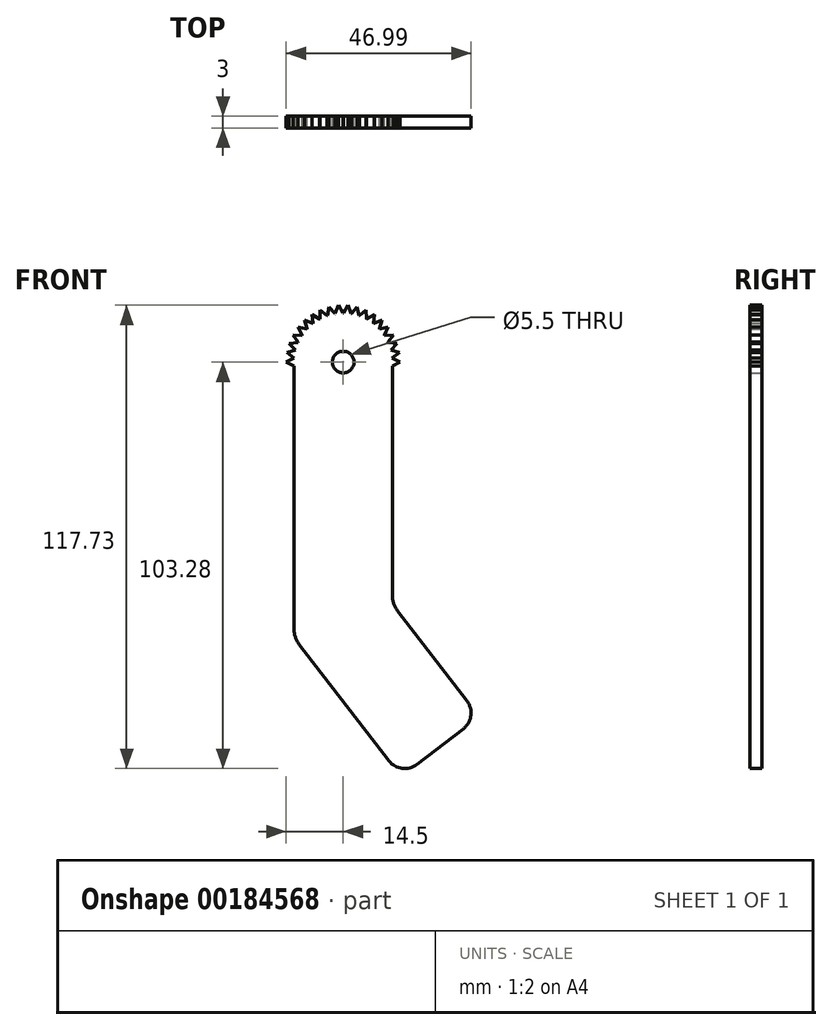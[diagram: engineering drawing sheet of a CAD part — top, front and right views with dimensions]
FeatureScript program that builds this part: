
annotation { "Feature Type Name" : "Feature", "Feature Type Description" : "" }
export const myFeature = defineFeature(function(context is Context, id is Id, definition is map)
    precondition{}
    {
        {
            var Q0;
            Q0=qCreatedBy(makeId("Front.planeOp"),FACE);
            var sketch = newSketch(context, id + "F0", { "sketchPlane" : qUnion([Q0])});
            skCircle(sketch, "E0", {"center": v(0, 0) * mm, "radius": 12.5 * mm});
            skLineSegment(sketch, "E1", {"start": v(-12.5, 0) * mm, "end": v(-12.5, -67.84) * mm});
            skLineSegment(sketch, "E2", {"start": v(-11.18, -71.71) * mm, "end": v(26.36, -120.4) * mm});
            skLineSegment(sketch, "E3", {"start": v(35.27, -121.56) * mm, "end": v(45.01, -114.05) * mm});
            skLineSegment(sketch, "E4", {"start": v(46.16, -105.14) * mm, "end": v(13.82, -63.2) * mm});
            skLineSegment(sketch, "E5", {"start": v(12.5, -59.32) * mm, "end": v(12.5, 0) * mm});
            skLineSegment(sketch, "E6", {"start": v(12.5, 0) * mm, "end": v(14.5, 0) * mm});
            skLineSegment(sketch, "E7", {"start": v(14.5, 0) * mm, "end": v(12.46, 1) * mm});
            skLineSegment(sketch, "E8", {"start": v(12.46, 1) * mm, "end": v(12.46, -1) * mm});
            skLineSegment(sketch, "E9", {"start": v(12.46, -1) * mm, "end": v(14.5, 0) * mm});
            skLineSegment(sketch, "E10.1.0", {"start": v(14.3, 2.39) * mm, "end": v(12.13, 3.04) * mm});
            skLineSegment(sketch, "E10.1.1", {"start": v(12.45, 1.06) * mm, "end": v(14.3, 2.39) * mm});
            skLineSegment(sketch, "E10.1.2", {"start": v(12.13, 3.04) * mm, "end": v(12.45, 1.06) * mm});
            skLineSegment(sketch, "E10.1.3", {"start": v(12.33, 2.06) * mm, "end": v(14.3, 2.39) * mm});
            skLineSegment(sketch, "E10.2.0", {"start": v(13.71, 4.7) * mm, "end": v(11.46, 5) * mm});
            skLineSegment(sketch, "E10.2.1", {"start": v(12.1, 3.1) * mm, "end": v(13.71, 4.7) * mm});
            skLineSegment(sketch, "E10.2.2", {"start": v(11.46, 5) * mm, "end": v(12.1, 3.1) * mm});
            skLineSegment(sketch, "E10.2.3", {"start": v(11.82, 4.06) * mm, "end": v(13.71, 4.7) * mm});
            skLineSegment(sketch, "E10.3.0", {"start": v(12.75, 6.9) * mm, "end": v(10.48, 6.8) * mm});
            skLineSegment(sketch, "E10.3.1", {"start": v(11.43, 5.05) * mm, "end": v(12.75, 6.9) * mm});
            skLineSegment(sketch, "E10.3.2", {"start": v(10.48, 6.8) * mm, "end": v(11.43, 5.05) * mm});
            skLineSegment(sketch, "E10.3.3", {"start": v(11, 5.95) * mm, "end": v(12.75, 6.9) * mm});
            skLineSegment(sketch, "E10.4.0", {"start": v(11.44, 8.9) * mm, "end": v(9.22, 8.44) * mm});
            skLineSegment(sketch, "E10.4.1", {"start": v(10.45, 6.86) * mm, "end": v(11.44, 8.9) * mm});
            skLineSegment(sketch, "E10.4.2", {"start": v(9.22, 8.44) * mm, "end": v(10.45, 6.86) * mm});
            skLineSegment(sketch, "E10.4.3", {"start": v(9.86, 7.68) * mm, "end": v(11.44, 8.9) * mm});
            skLineSegment(sketch, "E10.5.0", {"start": v(9.82, 10.67) * mm, "end": v(7.7, 9.84) * mm});
            skLineSegment(sketch, "E10.5.1", {"start": v(9.17, 8.49) * mm, "end": v(9.82, 10.67) * mm});
            skLineSegment(sketch, "E10.5.2", {"start": v(7.7, 9.84) * mm, "end": v(9.17, 8.49) * mm});
            skLineSegment(sketch, "E10.5.3", {"start": v(8.47, 9.2) * mm, "end": v(9.82, 10.67) * mm});
            skLineSegment(sketch, "E10.6.0", {"start": v(7.93, 12.14) * mm, "end": v(5.98, 10.98) * mm});
            skLineSegment(sketch, "E10.6.1", {"start": v(7.65, 9.88) * mm, "end": v(7.93, 12.14) * mm});
            skLineSegment(sketch, "E10.6.2", {"start": v(5.98, 10.98) * mm, "end": v(7.65, 9.88) * mm});
            skLineSegment(sketch, "E10.6.3", {"start": v(6.84, 10.46) * mm, "end": v(7.93, 12.14) * mm});
            skLineSegment(sketch, "E10.7.0", {"start": v(5.82, 13.28) * mm, "end": v(4.09, 11.81) * mm});
            skLineSegment(sketch, "E10.7.1", {"start": v(5.92, 11) * mm, "end": v(5.82, 13.28) * mm});
            skLineSegment(sketch, "E10.7.2", {"start": v(4.09, 11.81) * mm, "end": v(5.92, 11) * mm});
            skLineSegment(sketch, "E10.7.3", {"start": v(5.02, 11.45) * mm, "end": v(5.82, 13.28) * mm});
            skLineSegment(sketch, "E10.8.0", {"start": v(3.56, 14.06) * mm, "end": v(2.09, 12.32) * mm});
            skLineSegment(sketch, "E10.8.1", {"start": v(4.03, 11.83) * mm, "end": v(3.56, 14.06) * mm});
            skLineSegment(sketch, "E10.8.2", {"start": v(2.09, 12.32) * mm, "end": v(4.03, 11.83) * mm});
            skLineSegment(sketch, "E10.8.3", {"start": v(3.07, 12.12) * mm, "end": v(3.56, 14.06) * mm});
            skLineSegment(sketch, "E10.9.0", {"start": v(1.2, 14.45) * mm, "end": v(0.03, 12.5) * mm});
            skLineSegment(sketch, "E10.9.1", {"start": v(2.03, 12.33) * mm, "end": v(1.2, 14.45) * mm});
            skLineSegment(sketch, "E10.9.2", {"start": v(0.03, 12.5) * mm, "end": v(2.03, 12.33) * mm});
            skLineSegment(sketch, "E10.9.3", {"start": v(1.03, 12.46) * mm, "end": v(1.2, 14.45) * mm});
            skLineSegment(sketch, "E10.10.0", {"start": v(-1.2, 14.45) * mm, "end": v(-2.03, 12.33) * mm});
            skLineSegment(sketch, "E10.10.1", {"start": v(-0.03, 12.5) * mm, "end": v(-1.2, 14.45) * mm});
            skLineSegment(sketch, "E10.10.2", {"start": v(-2.03, 12.33) * mm, "end": v(-0.03, 12.5) * mm});
            skLineSegment(sketch, "E10.10.3", {"start": v(-1.03, 12.46) * mm, "end": v(-1.2, 14.45) * mm});
            skLineSegment(sketch, "E10.11.0", {"start": v(-3.56, 14.06) * mm, "end": v(-4.03, 11.83) * mm});
            skLineSegment(sketch, "E10.11.1", {"start": v(-2.09, 12.32) * mm, "end": v(-3.56, 14.06) * mm});
            skLineSegment(sketch, "E10.11.2", {"start": v(-4.03, 11.83) * mm, "end": v(-2.09, 12.32) * mm});
            skLineSegment(sketch, "E10.11.3", {"start": v(-3.07, 12.12) * mm, "end": v(-3.56, 14.06) * mm});
            skLineSegment(sketch, "E10.12.0", {"start": v(-5.82, 13.28) * mm, "end": v(-5.92, 11) * mm});
            skLineSegment(sketch, "E10.12.1", {"start": v(-4.09, 11.81) * mm, "end": v(-5.82, 13.28) * mm});
            skLineSegment(sketch, "E10.12.2", {"start": v(-5.92, 11) * mm, "end": v(-4.09, 11.81) * mm});
            skLineSegment(sketch, "E10.12.3", {"start": v(-5.02, 11.45) * mm, "end": v(-5.82, 13.28) * mm});
            skLineSegment(sketch, "E10.13.0", {"start": v(-7.93, 12.14) * mm, "end": v(-7.65, 9.88) * mm});
            skLineSegment(sketch, "E10.13.1", {"start": v(-5.98, 10.98) * mm, "end": v(-7.93, 12.14) * mm});
            skLineSegment(sketch, "E10.13.2", {"start": v(-7.65, 9.88) * mm, "end": v(-5.98, 10.98) * mm});
            skLineSegment(sketch, "E10.13.3", {"start": v(-6.84, 10.46) * mm, "end": v(-7.93, 12.14) * mm});
            skLineSegment(sketch, "E10.14.0", {"start": v(-9.82, 10.67) * mm, "end": v(-9.17, 8.49) * mm});
            skLineSegment(sketch, "E10.14.1", {"start": v(-7.7, 9.84) * mm, "end": v(-9.82, 10.67) * mm});
            skLineSegment(sketch, "E10.14.2", {"start": v(-9.17, 8.49) * mm, "end": v(-7.7, 9.84) * mm});
            skLineSegment(sketch, "E10.14.3", {"start": v(-8.47, 9.2) * mm, "end": v(-9.82, 10.67) * mm});
            skLineSegment(sketch, "E10.15.0", {"start": v(-11.44, 8.9) * mm, "end": v(-10.45, 6.86) * mm});
            skLineSegment(sketch, "E10.15.1", {"start": v(-9.22, 8.44) * mm, "end": v(-11.44, 8.9) * mm});
            skLineSegment(sketch, "E10.15.2", {"start": v(-10.45, 6.86) * mm, "end": v(-9.22, 8.44) * mm});
            skLineSegment(sketch, "E10.15.3", {"start": v(-9.86, 7.68) * mm, "end": v(-11.44, 8.9) * mm});
            skLineSegment(sketch, "E10.16.0", {"start": v(-12.75, 6.9) * mm, "end": v(-11.43, 5.05) * mm});
            skLineSegment(sketch, "E10.16.1", {"start": v(-10.48, 6.8) * mm, "end": v(-12.75, 6.9) * mm});
            skLineSegment(sketch, "E10.16.2", {"start": v(-11.43, 5.05) * mm, "end": v(-10.48, 6.8) * mm});
            skLineSegment(sketch, "E10.16.3", {"start": v(-11, 5.95) * mm, "end": v(-12.75, 6.9) * mm});
            skLineSegment(sketch, "E10.17.0", {"start": v(-13.71, 4.7) * mm, "end": v(-12.1, 3.1) * mm});
            skLineSegment(sketch, "E10.17.1", {"start": v(-11.46, 5) * mm, "end": v(-13.71, 4.7) * mm});
            skLineSegment(sketch, "E10.17.2", {"start": v(-12.1, 3.1) * mm, "end": v(-11.46, 5) * mm});
            skLineSegment(sketch, "E10.17.3", {"start": v(-11.82, 4.06) * mm, "end": v(-13.71, 4.7) * mm});
            skLineSegment(sketch, "E10.18.0", {"start": v(-14.3, 2.39) * mm, "end": v(-12.45, 1.06) * mm});
            skLineSegment(sketch, "E10.18.1", {"start": v(-12.13, 3.04) * mm, "end": v(-14.3, 2.39) * mm});
            skLineSegment(sketch, "E10.18.2", {"start": v(-12.45, 1.06) * mm, "end": v(-12.13, 3.04) * mm});
            skLineSegment(sketch, "E10.18.3", {"start": v(-12.33, 2.06) * mm, "end": v(-14.3, 2.39) * mm});
            skLineSegment(sketch, "E10.19.0", {"start": v(-14.5, 0) * mm, "end": v(-12.46, -1) * mm});
            skLineSegment(sketch, "E10.19.1", {"start": v(-12.46, 1) * mm, "end": v(-14.5, 0) * mm});
            skLineSegment(sketch, "E10.19.2", {"start": v(-12.46, -1) * mm, "end": v(-12.46, 1) * mm});
            skLineSegment(sketch, "E10.19.3", {"start": v(-12.5, 0) * mm, "end": v(-14.5, 0) * mm});
            skLineSegment(sketch, "E10.anchor1", {"start": v(0, 0) * mm, "end": v(12.46, -1) * mm, "construction": true});
            skLineSegment(sketch, "E10.anchor2", {"start": v(0, 0) * mm, "end": v(-12.46, 1) * mm, "construction": true});
            skPoint(sketch, "E11.visualSharp", {"position": v(12.5, -61.48) * mm});
            skArc(sketch, "E11.filletArc", {"start": v(12.5, -59.32) * mm, "mid": v(12.84, -61.37) * mm, "end": v(13.82, -63.2) * mm});
            skPoint(sketch, "E12.visualSharp", {"position": v(-12.5, -70) * mm});
            skArc(sketch, "E12.filletArc", {"start": v(-12.5, -67.84) * mm, "mid": v(-12.16, -69.88) * mm, "end": v(-11.18, -71.71) * mm});
            skPoint(sketch, "E13.visualSharp", {"position": v(30.24, -125.44) * mm});
            skArc(sketch, "E13.filletArc", {"start": v(26.36, -120.4) * mm, "mid": v(30.58, -122.83) * mm, "end": v(35.27, -121.56) * mm});
            skPoint(sketch, "E14.visualSharp", {"position": v(50.04, -110.17) * mm});
            skArc(sketch, "E14.filletArc", {"start": v(45.01, -114.05) * mm, "mid": v(47.43, -109.83) * mm, "end": v(46.16, -105.14) * mm});
            skCircle(sketch, "E15", {"center": v(0, 0) * mm, "radius": 1.5 * mm});
            skSolve(sketch);
        }
        {
            var Q0;
            Q0=qSketchRegion(id+"F0",true);
            var Q1;
            Q1=makeQuery(id+"F0.imprint","IMPRINT",FACE,{"disambiguationData":[TD([[makeQuery(id+"F0.imprint","IMPRINT",EDGE,{"derivedFrom":sQuery(id+"F0.wireOp",EDGE,"E15")}),1.0]])]});
            extrude(context, id + "F1", {"entities" : qUnion([Q0, Q1]), "depth" : 3 * mm});
        }
        {
            var Q0;
            Q0=makeQuery(id+"F1.opExtrude","CAP_FACE",FACE,{"disambiguationData":[OSD([sQuery(id+"F0.wireOp",EDGE,"E0"),sQuery(id+"F0.wireOp",EDGE,"E1"),sQuery(id+"F0.wireOp",EDGE,"E2"),sQuery(id+"F0.wireOp",EDGE,"E3"),sQuery(id+"F0.wireOp",EDGE,"E4"),sQuery(id+"F0.wireOp",EDGE,"E5"),sQuery(id+"F0.wireOp",EDGE,"E7"),sQuery(id+"F0.wireOp",EDGE,"E9"),sQuery(id+"F0.wireOp",EDGE,"E10.1.0"),sQuery(id+"F0.wireOp",EDGE,"E10.1.1"),sQuery(id+"F0.wireOp",EDGE,"E10.2.0"),sQuery(id+"F0.wireOp",EDGE,"E10.2.1"),sQuery(id+"F0.wireOp",EDGE,"E10.3.0"),sQuery(id+"F0.wireOp",EDGE,"E10.3.1"),sQuery(id+"F0.wireOp",EDGE,"E10.4.0"),sQuery(id+"F0.wireOp",EDGE,"E10.4.1"),sQuery(id+"F0.wireOp",EDGE,"E10.5.0"),sQuery(id+"F0.wireOp",EDGE,"E10.5.1"),sQuery(id+"F0.wireOp",EDGE,"E10.6.0"),sQuery(id+"F0.wireOp",EDGE,"E10.6.1"),sQuery(id+"F0.wireOp",EDGE,"E10.7.0"),sQuery(id+"F0.wireOp",EDGE,"E10.7.1"),sQuery(id+"F0.wireOp",EDGE,"E10.8.0"),sQuery(id+"F0.wireOp",EDGE,"E10.8.1"),sQuery(id+"F0.wireOp",EDGE,"E10.9.0"),sQuery(id+"F0.wireOp",EDGE,"E10.9.1"),sQuery(id+"F0.wireOp",EDGE,"E10.10.0"),sQuery(id+"F0.wireOp",EDGE,"E10.10.1"),sQuery(id+"F0.wireOp",EDGE,"E10.11.0"),sQuery(id+"F0.wireOp",EDGE,"E10.11.1"),sQuery(id+"F0.wireOp",EDGE,"E10.12.0"),sQuery(id+"F0.wireOp",EDGE,"E10.12.1"),sQuery(id+"F0.wireOp",EDGE,"E10.13.0"),sQuery(id+"F0.wireOp",EDGE,"E10.13.1"),sQuery(id+"F0.wireOp",EDGE,"E10.14.0"),sQuery(id+"F0.wireOp",EDGE,"E10.14.1"),sQuery(id+"F0.wireOp",EDGE,"E10.15.0"),sQuery(id+"F0.wireOp",EDGE,"E10.15.1"),sQuery(id+"F0.wireOp",EDGE,"E10.16.0"),sQuery(id+"F0.wireOp",EDGE,"E10.16.1"),sQuery(id+"F0.wireOp",EDGE,"E10.17.0"),sQuery(id+"F0.wireOp",EDGE,"E10.17.1"),sQuery(id+"F0.wireOp",EDGE,"E10.18.0"),sQuery(id+"F0.wireOp",EDGE,"E10.18.1"),sQuery(id+"F0.wireOp",EDGE,"E10.19.0"),sQuery(id+"F0.wireOp",EDGE,"E10.19.1"),sQuery(id+"F0.wireOp",EDGE,"E11.filletArc"),sQuery(id+"F0.wireOp",EDGE,"E12.filletArc"),sQuery(id+"F0.wireOp",EDGE,"E13.filletArc"),sQuery(id+"F0.wireOp",EDGE,"E14.filletArc")])],"isStart":false});
            var sketch = newSketch(context, id + "F2", { "sketchPlane" : qUnion([Q0])});
            skLineSegment(sketch, "E16", {"start": v(0, 0) * mm, "end": v(0, -5) * mm});
            skLineSegment(sketch, "E17", {"start": v(0, -5) * mm, "end": v(0, -13.5) * mm});
            skCircle(sketch, "E18", {"center": v(0, -13.5) * mm, "radius": 1.5 * mm});
            skCircle(sketch, "E19", {"center": v(0, -5) * mm, "radius": 1.5 * mm});
            skSolve(sketch);
        }
        {
            var Q0;
            Q0=makeQuery(id+"F2.imprint","IMPRINT",FACE,{"disambiguationData":[TD([[makeQuery(id+"F2.imprint","IMPRINT",EDGE,{"derivedFrom":sQuery(id+"F2.wireOp",EDGE,"E18")}),-1.0]])]});
            var sketch = newSketch(context, id + "F3", { "sketchPlane" : qUnion([Q0])});
            skCircle(sketch, "E20", {"center": v(0, 0) * mm, "radius": 2.75 * mm});
            skSolve(sketch);
        }
        {
            var Q0;
            Q0=qSketchRegion(id+"F3",true);
            extrude(context, id + "F4", {"entities" : qUnion([Q0]), "operationType" : NewBodyOperationType.REMOVE, "endBound" : BoundingType.SYMMETRIC, "depth" : 762 * mm});
        }
        {
            var Q0;
            Q0=makeQuery(id+"F2.imprint","IMPRINT",FACE,{"disambiguationData":[TD([[makeQuery(id+"F2.imprint","IMPRINT",EDGE,{"derivedFrom":sQuery(id+"F2.wireOp",EDGE,"E18")}),-1.0]])]});
            var sketch = newSketch(context, id + "F5", { "sketchPlane" : qUnion([Q0])});
            skLineSegment(sketch, "E21", {"start": v(11.18, -108.06) * mm, "end": v(39.39, -86.31) * mm});
            skLineSegment(sketch, "E22", {"start": v(11.18, -108.06) * mm, "end": v(26.39, -126.6) * mm});
            skLineSegment(sketch, "E23", {"start": v(26.39, -126.6) * mm, "end": v(60.57, -109.77) * mm});
            skLineSegment(sketch, "E24", {"start": v(60.57, -109.77) * mm, "end": v(39.39, -86.31) * mm});
            skSolve(sketch);
        }
        {
            var Q0;
            Q0=qSketchRegion(id+"F5",true);
            extrude(context, id + "F6", {"entities" : qUnion([Q0]), "operationType" : NewBodyOperationType.REMOVE, "endBound" : BoundingType.SYMMETRIC, "oppositeDirection" : true, "depth" : 762 * mm});
        }
        {
            var Q0;
            Q0=makeQuery(id+"F6.boolean.opBoolean","INTERSECT",EDGE,{"derivedFrom":[makeQuery(id+"F1.opExtrude","SWEPT_FACE",FACE,{"disambiguationData":[OSD([sQuery(id+"F0.wireOp",EDGE,"E2")])]}),makeQuery(id+"F6.opExtrude","SWEPT_FACE",FACE,{"disambiguationData":[OSD([sQuery(id+"F5.wireOp",EDGE,"E21")])]})]});
            fillet(context, id + "F7", {"entities" : qUnion([Q0]), "radius" : 5.08 * mm, "tangentPropagation" : true, "allowEdgeOverflow" : false});
        }
        {
            var Q0;
            Q0=makeQuery(id+"F6.boolean.opBoolean","INTERSECT",EDGE,{"derivedFrom":[makeQuery(id+"F1.opExtrude","SWEPT_FACE",FACE,{"disambiguationData":[OSD([sQuery(id+"F0.wireOp",EDGE,"E4")])]}),makeQuery(id+"F6.opExtrude","SWEPT_FACE",FACE,{"disambiguationData":[OSD([sQuery(id+"F5.wireOp",EDGE,"E21")])]})]});
            fillet(context, id + "F8", {"entities" : qUnion([Q0]), "radius" : 5.08 * mm, "tangentPropagation" : true, "allowEdgeOverflow" : false});
        }
    });
